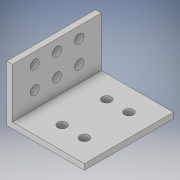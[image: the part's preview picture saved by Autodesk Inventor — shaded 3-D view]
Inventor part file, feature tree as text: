
AUTODESK INVENTOR PART (.ipt)
format: ipt  version: 2018 (Build 220112000, 112)  size: 160,768 bytes
history: native  units: in
note: dims shown in document units (in); Inventor stores cm internally (conversion verified against a paired STEP export)
features: extrude x3, sketch x3
ambient origin geometry x8: Origin, YZ Plane, XZ Plane, XY Plane, X Axis, Y Axis, Z Axis, Center Point
bodies: Solid1 (feature_tree)
feature tree (6):
  extrude  "Extrusion1"  Depth=0.13in
  extrude  "Extrusion3"  Depth=2.0in
  extrude  "Extrusion7"  Depth=1.25in
  sketch  "Sketch1"  dims[d1=0.13in d2=0.13in]
  sketch  "Sketch3"  dims[d4=2.0in d5=0.0in d9=0.5in]
  sketch  "Sketch4"  dims[d10=0.5in d11=0.5in d12=0.5in d13=0.5in d14=0.5in d15=0.5in d16=0.5in d17=0.5in d18=0.2031in d19=0.2031in d20=0.2031in d21=0.2031in d22=0.2031in d23=0.2031in d24=2.0in d25=0.0in d26=0.5in d27=0.25in d28=0.5in d29=0.5in d31=0.53in d33=0.2031in d34=0.2031in d37=0.25in d38=0.5in d39=0.5in d40=0.5in d42=0.2031in d43=0.2031in d50=1.75in d53=0.5in d57=1.25in d58=1.0in d59=0.0in]
